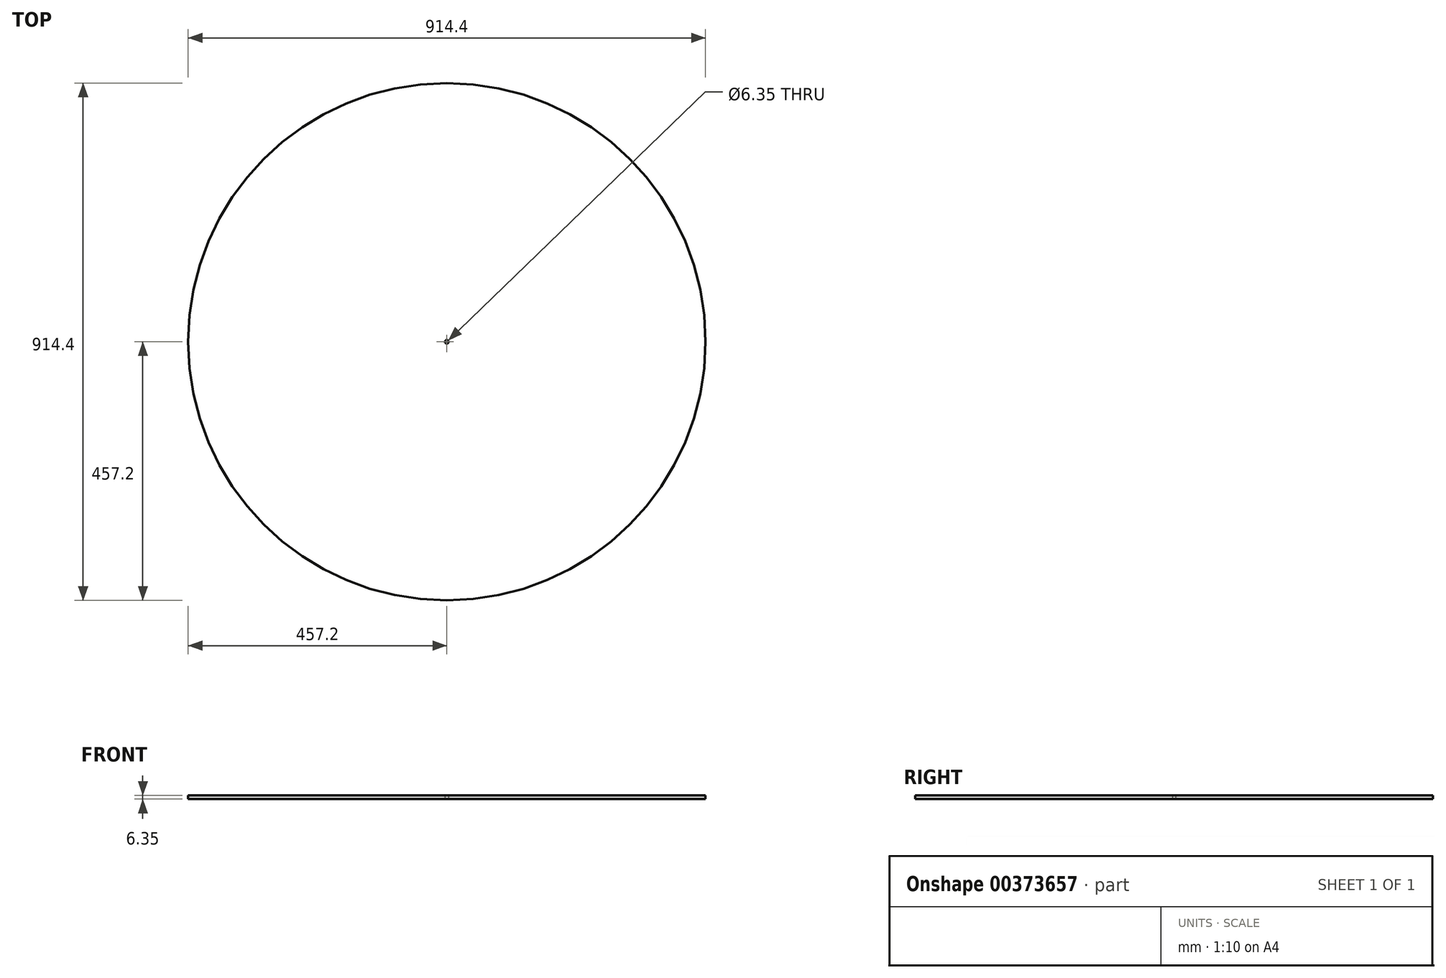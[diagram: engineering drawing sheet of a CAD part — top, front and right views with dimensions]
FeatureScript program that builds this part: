
annotation { "Feature Type Name" : "Feature", "Feature Type Description" : "" }
export const myFeature = defineFeature(function(context is Context, id is Id, definition is map)
    precondition{}
    {
        {
            var Q0;
            Q0=qCreatedBy(makeId("Top.planeOp"),FACE);
            var sketch = newSketch(context, id + "F0", { "sketchPlane" : qUnion([Q0])});
            skCircle(sketch, "E0", {"center": v(0, 0) * mm, "radius": 457.2 * mm});
            skCircle(sketch, "E1", {"center": v(0, 0) * mm, "radius": 3.18 * mm});
            skCircle(sketch, "E2", {"center": v(0, 0) * mm, "radius": 406.4 * mm});
            skSolve(sketch);
        }
        {
            var Q0;
            Q0=makeQuery(id+"F0.imprint","IMPRINT",FACE,{"disambiguationData":[TD([[makeQuery(id+"F0.imprint","IMPRINT",EDGE,{"derivedFrom":sQuery(id+"F0.wireOp",EDGE,"E0")}),1.0]])]});
            var Q1;
            Q1=makeQuery(id+"F0.imprint","IMPRINT",FACE,{"disambiguationData":[TD([[makeQuery(id+"F0.imprint","IMPRINT",EDGE,{"derivedFrom":sQuery(id+"F0.wireOp",EDGE,"E1")}),-1.0]])]});
            extrude(context, id + "F1", {"entities" : qUnion([Q0, Q1]), "depth" : 6.35 * mm});
        }
    });
